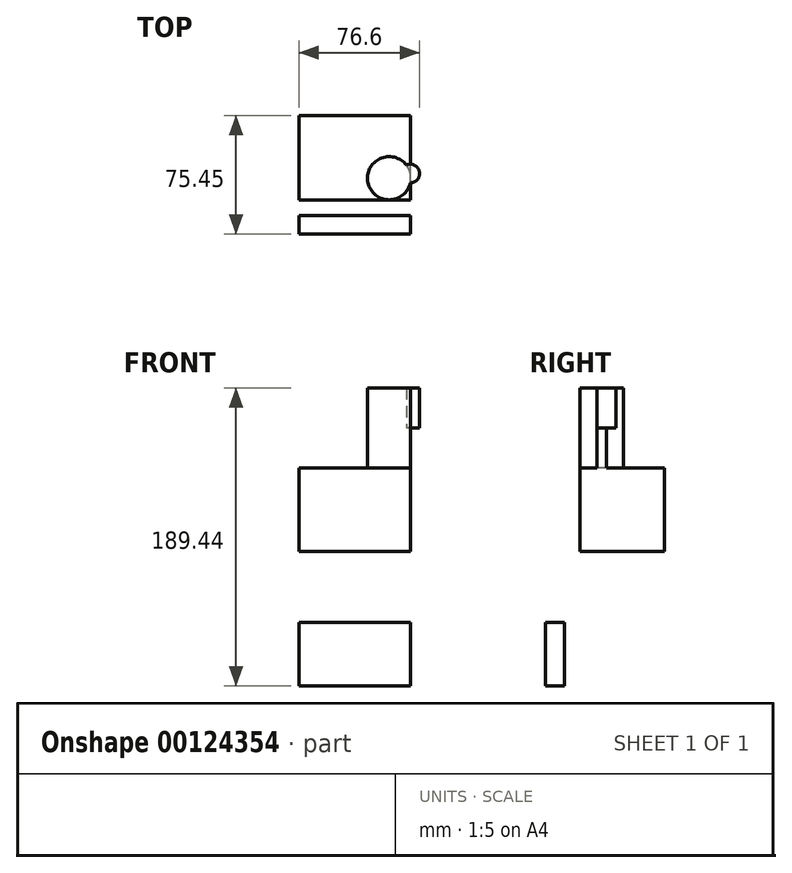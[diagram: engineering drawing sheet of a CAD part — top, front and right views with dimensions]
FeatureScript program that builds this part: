
annotation { "Feature Type Name" : "Feature", "Feature Type Description" : "" }
export const myFeature = defineFeature(function(context is Context, id is Id, definition is map)
    precondition{}
    {
        {
            var Q0;
            Q0=qCreatedBy(makeId("Right.planeOp"),FACE);
            var sketch = newSketch(context, id + "F3", { "sketchPlane" : qUnion([Q0])});
            skLineSegment(sketch, "E0.bottom", {"start": v(-41.53, -30.55) * mm, "end": v(-53.53, -30.55) * mm});
            skLineSegment(sketch, "E0.top", {"start": v(-41.53, -70.92) * mm, "end": v(-53.53, -70.92) * mm});
            skLineSegment(sketch, "E0.left", {"start": v(-41.53, -30.55) * mm, "end": v(-41.53, -70.92) * mm});
            skLineSegment(sketch, "E0.right", {"start": v(-53.53, -30.55) * mm, "end": v(-53.53, -70.92) * mm});
            skLineSegment(sketch, "E1.bottom", {"start": v(-31.66, 14.59) * mm, "end": v(21.92, 14.59) * mm});
            skLineSegment(sketch, "E1.top", {"start": v(-31.66, 67.72) * mm, "end": v(21.92, 67.72) * mm});
            skLineSegment(sketch, "E1.left", {"start": v(-31.66, 14.59) * mm, "end": v(-31.66, 67.72) * mm});
            skLineSegment(sketch, "E1.right", {"start": v(21.92, 14.59) * mm, "end": v(21.92, 67.72) * mm});
            skSolve(sketch);
        }
        {
            var Q0;
            Q0 = qSketchRegion(id + "F3", true);
            extrude(context, id + "F0", {"entities" : qUnion([Q0]), "depth" : 70.65 * mm});
        }
        {
            var Q0;
            Q0=makeQuery(id+"F0.opExtrude","SWEPT_FACE",FACE,{"disambiguationData":[OSD([sQuery(id+"F3.wireOp",EDGE,"E1.top")])]});
            var sketch = newSketch(context, id + "F1", { "sketchPlane" : qUnion([Q0])});
            skCircle(sketch, "E2", {"center": v(40.62, -4.87) * mm, "radius": 7.19 * mm});
            skPoint(sketch, "E2.centerSnap0", {"position": v(70.65, -4.87) * mm});
            skCircle(sketch, "E3", {"center": v(57.24, -17.92) * mm, "radius": 13.74 * mm});
            skSolve(sketch);
        }
        {
            var Q0;
            {var subQ0=sQuery(id+"F1.wireOp",EDGE,"E3");var subQ1=sQuery(id+"F3.wireOp",EDGE,"E1.top");var subQ3=makeQuery(id+"F0.opExtrude","CAP_EDGE",EDGE,{"disambiguationData":[OSD([subQ1])],"isStart":false});var subQ4=makeQuery(id+"F1.imprint","INTERSECT",VERTEX,{"disambiguationData":[OD(0.0)],"derivedFrom":[subQ3,subQ0]});Q0=makeQuery(id+"F1.imprint","IMPRINT",FACE,{"disambiguationData":[TD([[makeQuery(id+"F1.imprint","IMPRINT",EDGE,{"disambiguationData":[TD([[subQ4,1.0]])],"derivedFrom":subQ3}),1.0]])]});}
            extrude(context, id + "F4", {"entities" : qUnion([Q0]), "operationType" : NewBodyOperationType.ADD, "depth" : 25.4 * mm});
        }
        {
            var Q0;
            Q0=makeQuery(id+"F4.opExtrude","CAP_FACE",FACE,{"disambiguationData":[OSD([sQuery(id+"F3.wireOp",EDGE,"E1.top"),sQuery(id+"F1.wireOp",EDGE,"E3")])],"isStart":false});
            var sketch = newSketch(context, id + "F2", { "sketchPlane" : qUnion([Q0])});
            skCircle(sketch, "E4", {"center": v(70.65, -14.95) * mm, "radius": 5.95 * mm});
            skSolve(sketch);
        }
        {
            var Q0;
            Q0 = qSketchRegion(id + "F2", true);
            var Q1;
            {var subQ0=sQuery(id+"F2.wireOp",EDGE,"E4");var subQ1=makeQuery(id+"F4.opExtrude","CAP_EDGE",EDGE,{"disambiguationData":[OSD([sQuery(id+"F1.wireOp",EDGE,"E3")])],"isStart":false});var subQ3=makeQuery(id+"F2.imprint","INTERSECT",VERTEX,{"derivedFrom":[subQ1,subQ0]});Q1=makeQuery(id+"F2.imprint","IMPRINT",FACE,{"disambiguationData":[TD([[makeQuery(id+"F2.imprint","IMPRINT",EDGE,{"disambiguationData":[TD([[subQ3,-1.0]])],"derivedFrom":subQ0}),-1.0]])]});}
            extrude(context, id + "F5", {"entities" : qUnion([Q0, Q1]), "operationType" : NewBodyOperationType.ADD, "depth" : 25.4 * mm});
        }
    });
